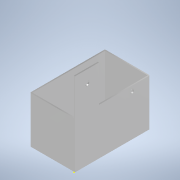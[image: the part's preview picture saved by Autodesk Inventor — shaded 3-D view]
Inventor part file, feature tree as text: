
AUTODESK INVENTOR PART (.ipt)
format: ipt  version: 2021 (Build 250183000, 183)  size: 207,872 bytes
history: native  units: mm
features: sketch x10, extrude x6, hole x3, fillet x2, chamfer x1, projected_geometry x1
ambient origin geometry x8: Origin, YZ Plane, XZ Plane, XY Plane, X Axis, Y Axis, Z Axis, Center Point
bodies: Solid1 (feature_tree)
feature tree (23):
  extrude  "base"  Depth=188.0mm
  extrude  "walls"  Depth=3.0mm
  extrude  "Extrusion8"  Depth=115.0mm
  hole  "Hole4"  [1 undecoded]
  fillet  "Fillet2"  Radius=54.0mm
  extrude  "Extrusion9"  TaperAngle=120.0deg  [1 undecoded]
  fillet  "Fillet3"  [1 undecoded]
  extrude  "Extrusion11"  Depth=1.0mm
  chamfer  "Chamfer4"  Distance=50.0mm
  sketch  "Sketch19"  dims[d103=6.0mm d104=8.0mm d105=4.0mm d106=2.0mm d107=90.0deg d108=8.0mm d109=20.594885mm d110=1.0mm]
  extrude  "Extrusion12"  Depth=30.0mm
  hole  "Hole6"  [1 undecoded]
  hole  "Hole7"  [1 undecoded]
  sketch  "Sketch1"  dims[d0=3.0mm d1=0.0mm d26=188.0mm]
  sketch  "Sketch7"  dims[d27=113.0mm d29=3.0mm]
  projected_geometry  "Projected Loop2"
  sketch  "Sketch13"  dims[d30=115.0mm d31=0.0mm d72=36.0mm d73=28.0mm]
  sketch  "Sketch14"  dims[d93=3.0mm d94=65.0mm d96=54.0mm d97=0.0mm]
  sketch  "Sketch15"  dims[d98=36.0mm d99=120.0deg d100=120.0deg]
  sketch  "Sketch17"  dims[d101=36.0mm]
  sketch  "Sketch20"  dims[d111=25.0mm d112=50.0mm d113=0.0mm]
  sketch  "Sketch21"  dims[d114=30.0mm d115=36.0mm]
  sketch  "Sketch22"  dims[d116=30.0mm d117=30.0mm d128=3.0mm d129=0.0mm d130=1.5mm d131=2.0mm d132=45.0deg d150=65.0mm d151=60.0mm d152=92.0mm d153=0.0mm d154=30.0mm d155=30.0mm d156=12.0mm d157=6.0mm d158=4.0mm d159=2.0mm d160=90.0deg d161=8.0mm d162=20.594885mm d163=12.0mm d164=45.0mm d165=10.0mm d166=6.0mm d167=4.0mm d168=2.0mm d169=90.0deg d170=8.0mm d171=20.594885mm]
note: 5 required parameter values undecoded (feature->parameter linkage not recoverable at this tier; creation-order binding heuristic only, values carry confidence <= 0.55)
